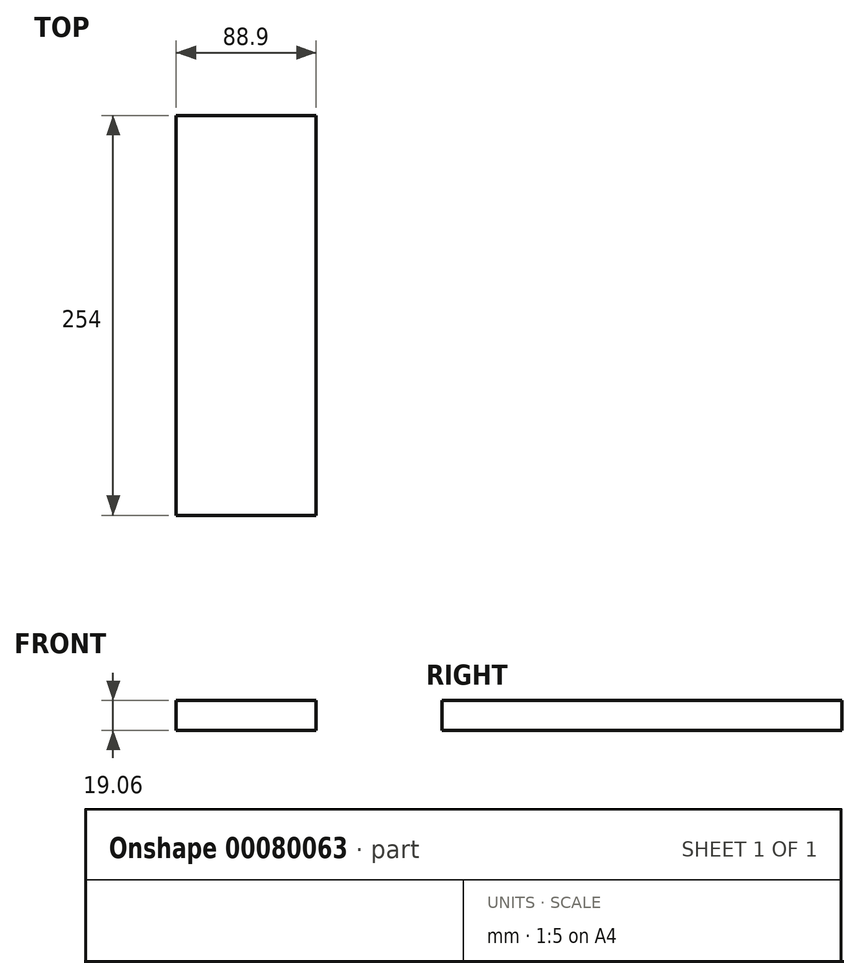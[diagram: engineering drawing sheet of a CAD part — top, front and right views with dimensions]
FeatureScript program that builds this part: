
annotation { "Feature Type Name" : "Feature", "Feature Type Description" : "" }
export const myFeature = defineFeature(function(context is Context, id is Id, definition is map)
    precondition{}
    {
        {
            var Q0;
            Q0=qCreatedBy(makeId("Front.planeOp"),FACE);
            var sketch = newSketch(context, id + "F0", { "sketchPlane" : qUnion([Q0])});
            skLineSegment(sketch, "E0.bottom", {"start": v(-44.45, 9.52) * mm, "end": v(44.45, 9.52) * mm});
            skLineSegment(sketch, "E0.top", {"start": v(-44.45, -9.52) * mm, "end": v(44.45, -9.52) * mm});
            skLineSegment(sketch, "E0.left", {"start": v(-44.45, 9.52) * mm, "end": v(-44.45, -9.52) * mm});
            skLineSegment(sketch, "E0.right", {"start": v(44.45, 9.52) * mm, "end": v(44.45, -9.52) * mm});
            skPoint(sketch, "E0.middle", {"position": v(0, 0) * mm});
            skSolve(sketch);
        }
        {
            var Q0;
            Q0=makeQuery(id+"F0.imprint","IMPRINT",FACE,{"disambiguationData":[TD([[makeQuery(id+"F0.imprint","IMPRINT",EDGE,{"derivedFrom":sQuery(id+"F0.wireOp",EDGE,"E0.bottom")}),-1.0]])]});
            extrude(context, id + "F1", {"entities" : qUnion([Q0]), "endBound" : BoundingType.SYMMETRIC, "depth" : 254 * mm});
        }
    });
